# Revit family: Podajnik_recznikow_w_roli JET
name_source: partatom
category: Furniture
units: mm (PartAtom-declared; Revit-internal decimal feet)

## family parameters
Always vertical = Yes
Cut with Voids When Loaded = No
Host = Wall
Room Calculation Point = No
Shared = No

## types (1)
- Type 1
    Color / Kolor = Szary / transparentny (jasny)
    Depth / Glebokosc = 210 mm  [stored 0.688976 ft]
    Description = odajnik ręczników w roli JET wykonany jest z trwałego plastiku ABS. Idealnie nadaje się do toalet publicznych, gabinetów lekarskich i punktów gastronomicznych. Gwarantuje wysoki poziom higieny, dzięki wygodnemu dozowaniu papieru, bez konieczności dotykania podajnika. Jego transparentna obudowa umożliwia bardzo prostą kontrolę zużycia rolki. Pojemnik na ręczniki papierowe JET jest uniwersalnym i wysoce funkcjonalnym urządzeniem.
    Height / Wysokosc = 310 mm  [stored 1.01706 ft]
    Manufacturer = FANECO.com
    Manufacturer code / Kod producenta = 5901764291930
    Material finish / Wykonczenie = Plastic ABS
    Model = JET
    Product code / Kod produktu = P22PGWT
    Type Comments = Podajnik ręczników w roli JET
    URL = https://faneco.com
    Weight / Waga = 0.95 kg
    Width / Szerokosc = 220 mm  [stored 0.721785 ft]

note: [stored X ft] marks values corroborated as IEEE doubles in the binary element streams (Revit-internal decimal feet)

## geometry (parser evidence)
native form markers: Sweep x10
no freeform markers — native parametric forms only
